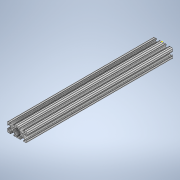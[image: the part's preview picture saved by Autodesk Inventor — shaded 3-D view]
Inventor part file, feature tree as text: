
AUTODESK INVENTOR PART (.ipt)
format: ipt  version: 2020 (Build 240168000, 168)  size: 333,824 bytes
history: native  units: in
note: dims shown in document units (in); Inventor stores cm internally (conversion verified against a paired STEP export)
features: sketch x2, extrude x1
ambient origin geometry x8: Origin, YZ Plane, XZ Plane, XY Plane, X Axis, Y Axis, Z Axis, Center Point
bodies: Solid1 (feature_tree)
feature tree (3):
  extrude  "Extrusion1"  [1 undecoded]
  sketch  "Sketch2"
  sketch  "Sketch1"  dims[d0=15.0in d1=0.0in]
note: 1 required parameter value undecoded (feature->parameter linkage not recoverable at this tier; creation-order binding heuristic only, values carry confidence <= 0.55)
